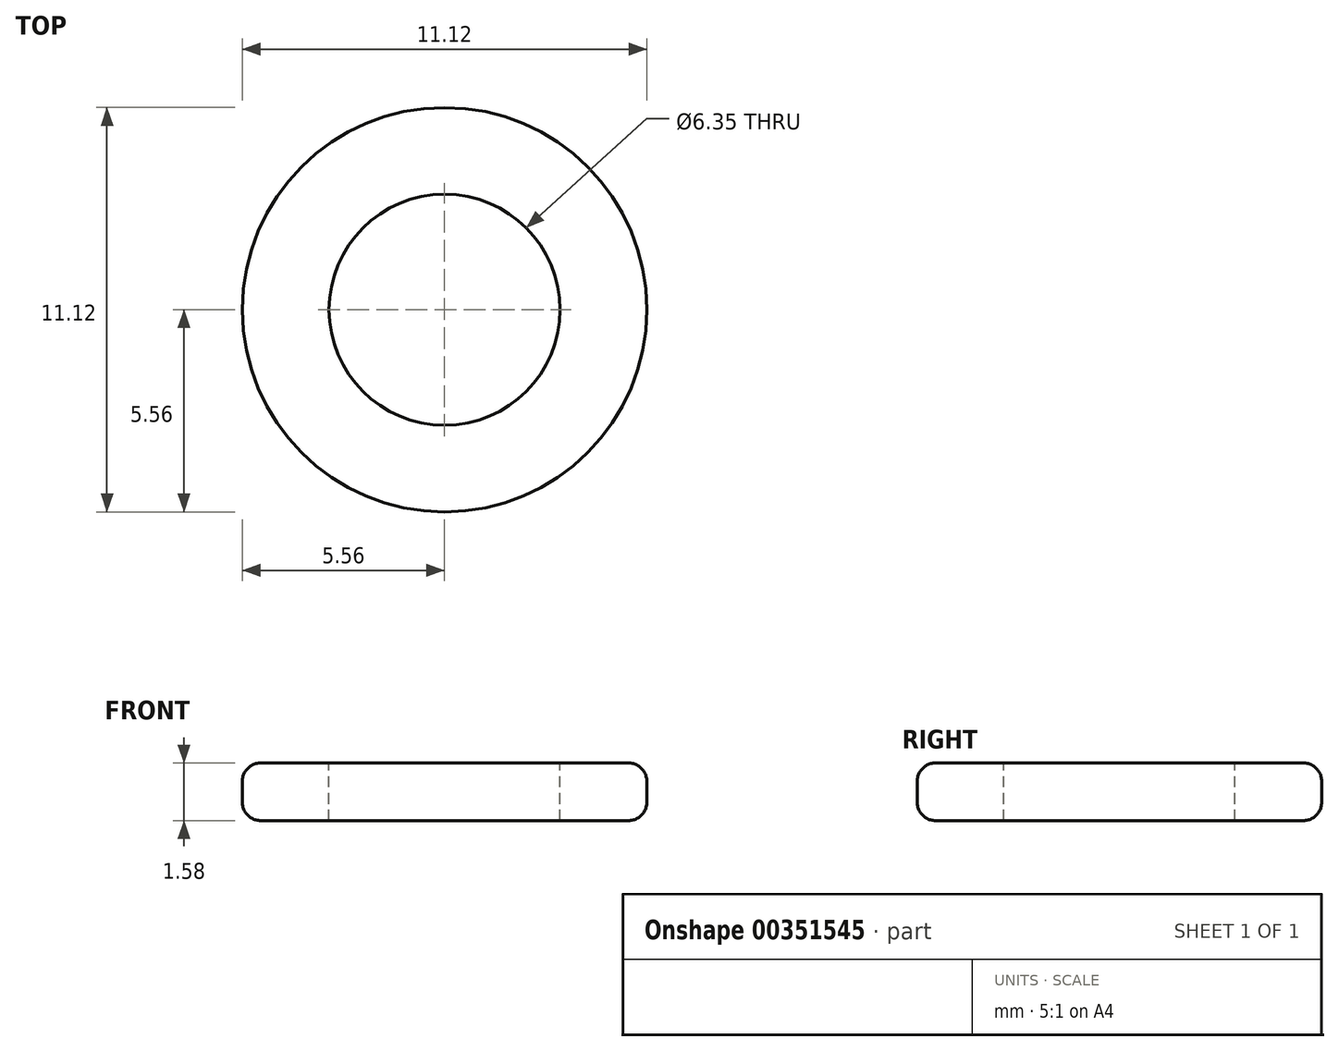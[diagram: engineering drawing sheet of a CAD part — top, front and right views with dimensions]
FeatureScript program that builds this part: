
annotation { "Feature Type Name" : "Feature", "Feature Type Description" : "" }
export const myFeature = defineFeature(function(context is Context, id is Id, definition is map)
    precondition{}
    {
        {
            var Q0;
            Q0=qCreatedBy(makeId("Top.planeOp"),FACE);
            var sketch = newSketch(context, id + "F0", { "sketchPlane" : qUnion([Q0])});
            skCircle(sketch, "E0", {"center": v(0, 0) * mm, "radius": 5.56 * mm});
            skSolve(sketch);
        }
        {
            var Q0;
            Q0 = qSketchRegion(id + "F0", true);
            extrude(context, id + "F1", {"entities" : qUnion([Q0]), "depth" : 1.59 * mm, "symmetric" : true});
        }
        {
            var Q0;
            Q0=makeQuery(id+"F1.opExtrude","CAP_FACE",FACE,{"disambiguationData":[OSD([sQuery(id+"F0.wireOp",EDGE,"E0")])],"isStart":false});
            var sketch = newSketch(context, id + "F2", { "sketchPlane" : qUnion([Q0])});
            skCircle(sketch, "E1", {"center": v(0, 0) * mm, "radius": 3.18 * mm});
            skSolve(sketch);
        }
        {
            var Q0;
            Q0 = qSketchRegion(id + "F2", true);
            extrude(context, id + "F3", {"entities" : qUnion([Q0]), "operationType" : NewBodyOperationType.REMOVE, "endBound" : BoundingType.THROUGH_ALL, "oppositeDirection" : true, "depth" : 25.4 * mm});
        }
        {
            var Q0;
            Q0=makeQuery(id+"F1.opExtrude","CAP_EDGE",EDGE,{"disambiguationData":[OSD([sQuery(id+"F0.wireOp",EDGE,"E0")])],"isStart":false});
            var Q1;
            Q1=makeQuery(id+"F1.opExtrude","CAP_EDGE",EDGE,{"disambiguationData":[OSD([sQuery(id+"F0.wireOp",EDGE,"E0")])],"isStart":true});
            fillet(context, id + "F4", {"entities" : qUnion([Q0, Q1]), "radius" : 0.5 * mm, "tangentPropagation" : true, "allowEdgeOverflow" : false});
        }
    });
